# Revit family: ACSQ-Round
name_source: partatom
category: Lighting Fixtures
revit_build: Autodesk Revit 2014 (Build: 20130308_1515(x64)
units: mm (PartAtom-declared; Revit-internal decimal feet)

## types (1)
- ACRD
    Apparent Load = 20 VA
    Assembly Code = D5020200
    Center Width = 3 "
    Certifications = The fixture is listed with ETL for outdoor, wet location use,
UL1598 and Canadian CSA Std. C22.2 no.250
    Color Temperature = 0 K
    Depth = 18.44 "
    Description = The Arts & Crafts® family of fixtures reflect the style and warmth of the Craftsman era. These fixtures are available in two sizes for post, wall or pendant mounting, as well as a matching bollard. The Arts & Crafts refractor system includes a symmetric and an asymmetric pattern to help control glare, while a wide variety of shade materials and finishes provides customization.
    Feaures = Full cutoff, dark sky compliant optical
system with solid shade
• Low angle beam has a maximum
candlepower at 65° for efficient spacing
between fixtures and control of glare
• Translucent shades add visual interest
when illuminated
• Pole, wall, and pendant mounting options
    Finish = Paint - Hubbell - Green Textured
    Fixture Height = 7.5 "
    Lamp = default
    Lens = Glass-Hubbell-Temper Molded
    Manufacturer = Hubbell Lighting
    Model = ACRD-PostTop
    Number of Poles = 1
    Offset From Pole = 6.12 "
    Photometric Notes = More IES files download on Photometric Web Link
    Photometric Web Link = https://www.hubbell.com
    Pole = Yes
    Pole Width = 4 "
    Power Factor = 1
    Product Documentation Link = https://hubbellcdn.com
    Product Page URL = https://www.hubbell.com
    Series = Arts & Crafts® Pedestrian
    Type Comments = Lighting Fixture
    URL = https://www.hubbell.com
    Voltage = 0 V
    Wattage Comments = 20W
    Width = 14 "

## geometry (parser evidence)
native form markers: Blend x2, Sweep x7
no freeform markers — native parametric forms only
